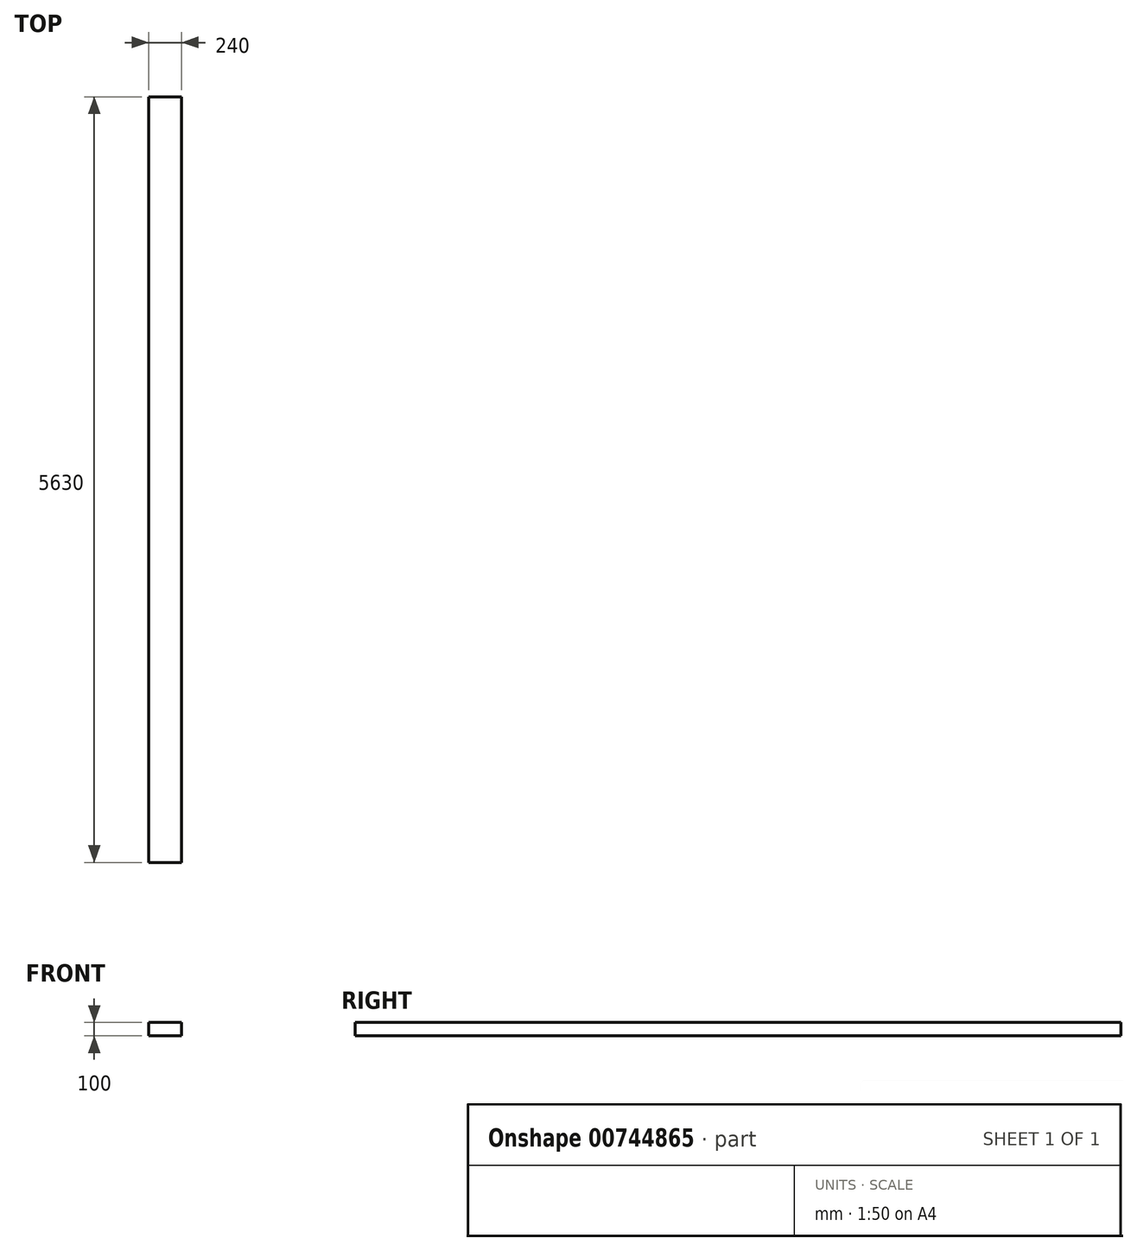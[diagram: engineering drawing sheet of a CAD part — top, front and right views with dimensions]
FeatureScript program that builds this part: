
annotation { "Feature Type Name" : "Feature", "Feature Type Description" : "" }
export const myFeature = defineFeature(function(context is Context, id is Id, definition is map)
    precondition{}
    {
        {
            var Q0;
            Q0=qCreatedBy(makeId("Front.planeOp"),FACE);
            var sketch = newSketch(context, id + "F0", { "sketchPlane" : qUnion([Q0])});
            skLineSegment(sketch, "E0.bottom", {"start": v(0, 0) * mm, "end": v(240, 0) * mm});
            skLineSegment(sketch, "E0.top", {"start": v(0, 100) * mm, "end": v(240, 100) * mm});
            skLineSegment(sketch, "E0.left", {"start": v(0, 0) * mm, "end": v(0, 100) * mm});
            skLineSegment(sketch, "E0.right", {"start": v(240, 0) * mm, "end": v(240, 100) * mm});
            skSolve(sketch);
        }
        {
            var Q0;
            Q0=makeQuery(id+"F0.imprint","IMPRINT",FACE,{"disambiguationData":[TD([[makeQuery(id+"F0.imprint","IMPRINT",EDGE,{"derivedFrom":sQuery(id+"F0.wireOp",EDGE,"E0.bottom")}),1.0]])]});
            extrude(context, id + "F1", {"entities" : qUnion([Q0]), "flatOperationType" : FlatOperationType.REMOVE, "depth" : 5630 * mm, "offsetDistance" : 25 * mm, "domain" : OperationDomain.MODEL});
        }
    });
